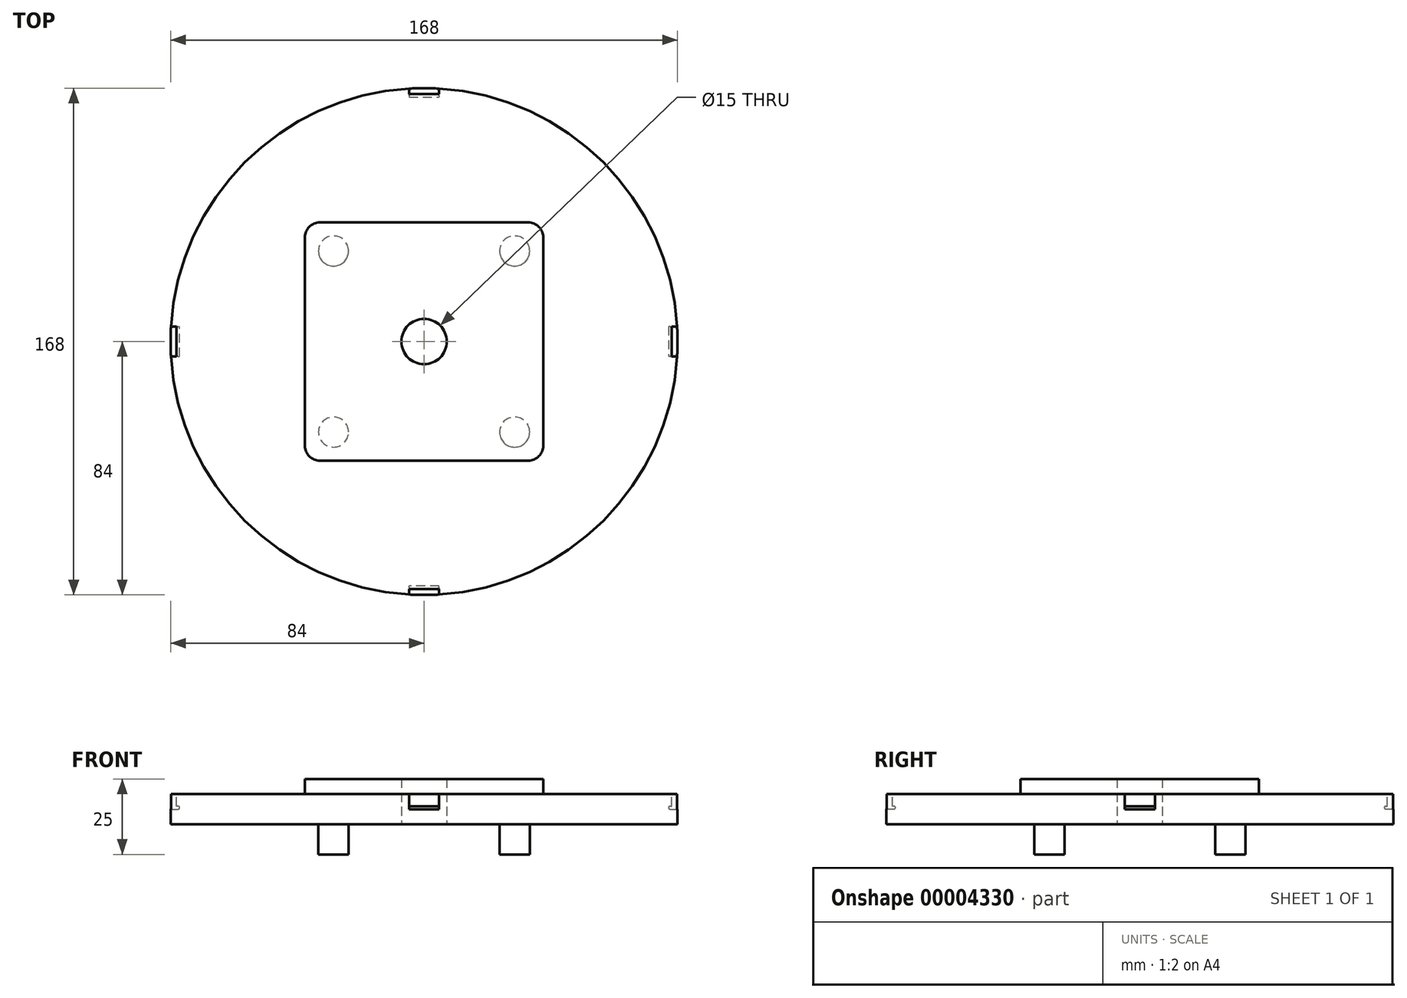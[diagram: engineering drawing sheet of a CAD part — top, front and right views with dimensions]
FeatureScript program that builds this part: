
annotation { "Feature Type Name" : "Feature", "Feature Type Description" : "" }
export const myFeature = defineFeature(function(context is Context, id is Id, definition is map)
    precondition{}
    {
        {
            var Q0;
            Q0=qCreatedBy(makeId("Top.planeOp"),FACE);
            var sketch = newSketch(context, id + "F0", { "sketchPlane" : qUnion([Q0])});
            skCircle(sketch, "E0", {"center": v(0, 0) * mm, "radius": 90 * mm});
            skSolve(sketch);
        }
        {
            var Q0;
            Q0=makeQuery(id+"F0.imprint","IMPRINT",FACE,{"disambiguationData":[TD([[makeQuery(id+"F0.imprint","IMPRINT",EDGE,{"derivedFrom":sQuery(id+"F0.wireOp",EDGE,"E0")}),1.0]])]});
            extrude(context, id + "F1", {"entities" : qUnion([Q0]), "depth" : 10 * mm});
        }
        {
            var Q0;
            Q0=makeQuery(id+"F1.opExtrude","CAP_FACE",FACE,{"disambiguationData":[OSD([sQuery(id+"F0.wireOp",EDGE,"E0")])],"isStart":false});
            var sketch = newSketch(context, id + "F2", { "sketchPlane" : qUnion([Q0])});
            skCircle(sketch, "E1.0", {"center": v(0, 0) * mm, "radius": 80 * mm});
            skLineSegment(sketch, "E2", {"start": v(0, 0) * mm, "end": v(-40, 0) * mm});
            skLineSegment(sketch, "E3", {"start": v(0, 0) * mm, "end": v(40, 0) * mm});
            skLineSegment(sketch, "E4", {"start": v(0, 0) * mm, "end": v(0, 40) * mm});
            skLineSegment(sketch, "E5", {"start": v(0, 0) * mm, "end": v(0, -40) * mm});
            skLineSegment(sketch, "E6", {"start": v(-40, -35) * mm, "end": v(-40, 35) * mm});
            skPoint(sketch, "E7.visualSharp", {"position": v(-40, 40) * mm});
            skLineSegment(sketch, "E8", {"start": v(40, 35) * mm, "end": v(40, -35) * mm});
            skPoint(sketch, "E9.visualSharp", {"position": v(40, 40) * mm});
            skPoint(sketch, "E10.visualSharp", {"position": v(40, -40) * mm});
            skPoint(sketch, "E11.visualSharp", {"position": v(-40, -40) * mm});
            skPoint(sketch, "E12.visualSharp", {"position": v(-40, -35) * mm});
            skPoint(sketch, "E13.visualSharp", {"position": v(40, -35) * mm});
            skPoint(sketch, "E14.visualSharp", {"position": v(40, 35) * mm});
            skPoint(sketch, "E15.visualSharp", {"position": v(-40, 35) * mm});
            skLineSegment(sketch, "E16.0", {"start": v(0, 40) * mm, "end": v(-35, 40) * mm});
            skLineSegment(sketch, "E17.0", {"start": v(0, 40) * mm, "end": v(35, 40) * mm});
            skLineSegment(sketch, "E18.0", {"start": v(0, -40) * mm, "end": v(35, -40) * mm});
            skLineSegment(sketch, "E19.0", {"start": v(0, -40) * mm, "end": v(-35, -40) * mm});
            skArc(sketch, "E20.filletArc", {"start": v(-40, -35) * mm, "mid": v(-38.54, -38.54) * mm, "end": v(-35, -40) * mm});
            skArc(sketch, "E21.filletArc", {"start": v(35, -40) * mm, "mid": v(38.54, -38.54) * mm, "end": v(40, -35) * mm});
            skArc(sketch, "E22.filletArc", {"start": v(40, 35) * mm, "mid": v(38.54, 38.54) * mm, "end": v(35, 40) * mm});
            skArc(sketch, "E23.filletArc", {"start": v(-35, 40) * mm, "mid": v(-38.54, 38.54) * mm, "end": v(-40, 35) * mm});
            skLineSegment(sketch, "E24.0", {"start": v(-39.5, -34.5) * mm, "end": v(-39.5, 34.5) * mm});
            skLineSegment(sketch, "E24.1", {"start": v(0, -39.5) * mm, "end": v(-34.5, -39.5) * mm});
            skLineSegment(sketch, "E24.2", {"start": v(0, -39.5) * mm, "end": v(34.5, -39.5) * mm});
            skLineSegment(sketch, "E24.3", {"start": v(39.5, 34.5) * mm, "end": v(39.5, -34.5) * mm});
            skLineSegment(sketch, "E24.4", {"start": v(0, 39.5) * mm, "end": v(34.5, 39.5) * mm});
            skLineSegment(sketch, "E24.5", {"start": v(0, 39.5) * mm, "end": v(-34.5, 39.5) * mm});
            skPoint(sketch, "E25.visualSharp", {"position": v(-39.5, 39.5) * mm});
            skArc(sketch, "E25.filletArc", {"start": v(-34.5, 39.5) * mm, "mid": v(-38.04, 38.04) * mm, "end": v(-39.5, 34.5) * mm});
            skPoint(sketch, "E26.visualSharp", {"position": v(-39.5, -39.5) * mm});
            skArc(sketch, "E26.filletArc", {"start": v(-39.5, -34.5) * mm, "mid": v(-38.04, -38.04) * mm, "end": v(-34.5, -39.5) * mm});
            skPoint(sketch, "E27.visualSharp", {"position": v(39.5, -39.5) * mm});
            skArc(sketch, "E27.filletArc", {"start": v(34.5, -39.5) * mm, "mid": v(38.04, -38.04) * mm, "end": v(39.5, -34.5) * mm});
            skPoint(sketch, "E28.visualSharp", {"position": v(39.5, 39.5) * mm});
            skArc(sketch, "E28.filletArc", {"start": v(39.5, 34.5) * mm, "mid": v(38.04, 38.04) * mm, "end": v(34.5, 39.5) * mm});
            skSolve(sketch);
        }
        {
            var Q0;
            Q0=makeQuery(id+"F1.opExtrude","CAP_FACE",FACE,{"disambiguationData":[OSD([sQuery(id+"F0.wireOp",EDGE,"E0")])],"isStart":true});
            var sketch = newSketch(context, id + "F3", { "sketchPlane" : qUnion([Q0])});
            skCircle(sketch, "E29.0", {"center": v(0, 0) * mm, "radius": 84 * mm});
            skSolve(sketch);
        }
        {
            var Q0;
            Q0=makeQuery(id+"F3.imprint","IMPRINT",FACE,{"disambiguationData":[TD([[makeQuery(id+"F3.imprint","IMPRINT",EDGE,{"derivedFrom":sQuery(id+"F3.wireOp",EDGE,"E29.0")}),-1.0]])]});
            extrude(context, id + "F4", {"entities" : qUnion([Q0]), "operationType" : NewBodyOperationType.REMOVE, "oppositeDirection" : true, "depth" : 25 * mm});
        }
        {
            var Q0;
            Q0=makeQuery(id+"F1.opExtrude","CAP_FACE",FACE,{"disambiguationData":[OSD([sQuery(id+"F0.wireOp",EDGE,"E0")])],"isStart":false});
            var sketch = newSketch(context, id + "F5", { "sketchPlane" : qUnion([Q0])});
            skLineSegment(sketch, "E30.0", {"start": v(5, 82) * mm, "end": v(-5, 82) * mm});
            skLineSegment(sketch, "E31.0", {"start": v(5, 84) * mm, "end": v(-5, 84) * mm});
            skLineSegment(sketch, "E32", {"start": v(-5, 84) * mm, "end": v(-5, 82) * mm});
            skLineSegment(sketch, "E33", {"start": v(5, 84) * mm, "end": v(5, 82) * mm});
            skLineSegment(sketch, "E34.0", {"start": v(-84, 5) * mm, "end": v(-84, -5) * mm});
            skLineSegment(sketch, "E35.0", {"start": v(-82, 5) * mm, "end": v(-82, -5) * mm});
            skLineSegment(sketch, "E36", {"start": v(-84, -5) * mm, "end": v(-82, -5) * mm});
            skLineSegment(sketch, "E37", {"start": v(-84, 5) * mm, "end": v(-82, 5) * mm});
            skLineSegment(sketch, "E38.0", {"start": v(5, -84) * mm, "end": v(-5, -84) * mm});
            skLineSegment(sketch, "E39.0", {"start": v(5, -82) * mm, "end": v(-5, -82) * mm});
            skLineSegment(sketch, "E40", {"start": v(-5, -82) * mm, "end": v(-5, -84) * mm});
            skLineSegment(sketch, "E41", {"start": v(5, -82) * mm, "end": v(5, -84) * mm});
            skLineSegment(sketch, "E42.0", {"start": v(84, 5) * mm, "end": v(84, -5) * mm});
            skLineSegment(sketch, "E43.0", {"start": v(82, 5) * mm, "end": v(82, -5) * mm});
            skLineSegment(sketch, "E44", {"start": v(82, -5) * mm, "end": v(84, -5) * mm});
            skLineSegment(sketch, "E45", {"start": v(82, 5) * mm, "end": v(84, 5) * mm});
            skSolve(sketch);
        }
        {
            var Q0;
            {var subQ2=sQuery(id+"F2.wireOp",EDGE,"E2");Q0=makeQuery(id+"F2.imprint","IMPRINT",FACE,{"disambiguationData":[TD([[makeQuery(id+"F2.imprint","IMPRINT",EDGE,{"derivedFrom":subQ2}),-1.0]])]});}
            var Q1;
            {var subQ2=sQuery(id+"F2.wireOp",EDGE,"E3");Q1=makeQuery(id+"F2.imprint","IMPRINT",FACE,{"disambiguationData":[TD([[makeQuery(id+"F2.imprint","IMPRINT",EDGE,{"derivedFrom":subQ2}),1.0]])]});}
            var Q2;
            {var subQ2=sQuery(id+"F2.wireOp",EDGE,"E3");Q2=makeQuery(id+"F2.imprint","IMPRINT",FACE,{"disambiguationData":[TD([[makeQuery(id+"F2.imprint","IMPRINT",EDGE,{"derivedFrom":subQ2}),-1.0]])]});}
            var Q3;
            {var subQ2=sQuery(id+"F2.wireOp",EDGE,"E2");Q3=makeQuery(id+"F2.imprint","IMPRINT",FACE,{"disambiguationData":[TD([[makeQuery(id+"F2.imprint","IMPRINT",EDGE,{"derivedFrom":subQ2}),1.0]])]});}
            extrude(context, id + "F6", {"entities" : qUnion([Q0, Q1, Q2, Q3]), "operationType" : NewBodyOperationType.ADD, "depth" : 5 * mm});
        }
        {
            var Q0;
            Q0=makeQuery(id+"F1.opExtrude","CAP_FACE",FACE,{"disambiguationData":[OSD([sQuery(id+"F0.wireOp",EDGE,"E0")])],"isStart":true});
            var sketch = newSketch(context, id + "F7", { "sketchPlane" : qUnion([Q0])});
            skLineSegment(sketch, "E46", {"start": v(0, 0) * mm, "end": v(0, 30) * mm});
            skLineSegment(sketch, "E47", {"start": v(0, 0) * mm, "end": v(0, -30) * mm});
            skLineSegment(sketch, "E48", {"start": v(0, 0) * mm, "end": v(-30, 0) * mm});
            skLineSegment(sketch, "E49", {"start": v(0, 0) * mm, "end": v(30, 0) * mm});
            skLineSegment(sketch, "E50.0", {"start": v(30, 0) * mm, "end": v(30, 30) * mm});
            skLineSegment(sketch, "E51.0", {"start": v(-30, 0) * mm, "end": v(-30, 30) * mm});
            skLineSegment(sketch, "E52.0", {"start": v(0, 30) * mm, "end": v(-30, 30) * mm});
            skLineSegment(sketch, "E53.0", {"start": v(0, 30) * mm, "end": v(30, 30) * mm});
            skLineSegment(sketch, "E54.0", {"start": v(-30, 0) * mm, "end": v(-30, -30) * mm});
            skLineSegment(sketch, "E55.0", {"start": v(30, 0) * mm, "end": v(30, -30) * mm});
            skLineSegment(sketch, "E56.0", {"start": v(0, -30) * mm, "end": v(-30, -30) * mm});
            skLineSegment(sketch, "E57.0", {"start": v(0, -30) * mm, "end": v(30, -30) * mm});
            skCircle(sketch, "E58", {"center": v(-30, 30) * mm, "radius": 5 * mm});
            skCircle(sketch, "E59", {"center": v(30, 30) * mm, "radius": 5 * mm});
            skCircle(sketch, "E60", {"center": v(-30, -30) * mm, "radius": 5 * mm});
            skCircle(sketch, "E61", {"center": v(30, -30) * mm, "radius": 5 * mm});
            skSolve(sketch);
        }
        {
            var Q0;
            {var subQ1=sQuery(id+"F7.wireOp",EDGE,"E52.0");var subQ3=sQuery(id+"F7.wireOp",EDGE,"E51.0");var subQ5=makeQuery(id+"F7.imprint","INTERSECT",VERTEX,{"derivedFrom":[subQ3,subQ1]});Q0=makeQuery(id+"F7.imprint","IMPRINT",FACE,{"disambiguationData":[TD([[makeQuery(id+"F7.imprint","IMPRINT",EDGE,{"disambiguationData":[TD([[subQ5,1.0]])],"derivedFrom":subQ3}),1.0]])]});}
            var Q1;
            {var subQ1=sQuery(id+"F7.wireOp",EDGE,"E52.0");var subQ3=sQuery(id+"F7.wireOp",EDGE,"E51.0");var subQ5=makeQuery(id+"F7.imprint","INTERSECT",VERTEX,{"derivedFrom":[subQ3,subQ1]});Q1=makeQuery(id+"F7.imprint","IMPRINT",FACE,{"disambiguationData":[TD([[makeQuery(id+"F7.imprint","IMPRINT",EDGE,{"disambiguationData":[TD([[subQ5,1.0]])],"derivedFrom":subQ3}),-1.0]])]});}
            var Q2;
            {var subQ1=sQuery(id+"F7.wireOp",EDGE,"E53.0");var subQ3=sQuery(id+"F7.wireOp",EDGE,"E50.0");var subQ5=makeQuery(id+"F7.imprint","INTERSECT",VERTEX,{"derivedFrom":[subQ3,subQ1]});Q2=makeQuery(id+"F7.imprint","IMPRINT",FACE,{"disambiguationData":[TD([[makeQuery(id+"F7.imprint","IMPRINT",EDGE,{"disambiguationData":[TD([[subQ5,1.0]])],"derivedFrom":subQ3}),-1.0]])]});}
            var Q3;
            {var subQ1=sQuery(id+"F7.wireOp",EDGE,"E53.0");var subQ3=sQuery(id+"F7.wireOp",EDGE,"E50.0");var subQ5=makeQuery(id+"F7.imprint","INTERSECT",VERTEX,{"derivedFrom":[subQ3,subQ1]});Q3=makeQuery(id+"F7.imprint","IMPRINT",FACE,{"disambiguationData":[TD([[makeQuery(id+"F7.imprint","IMPRINT",EDGE,{"disambiguationData":[TD([[subQ5,1.0]])],"derivedFrom":subQ3}),1.0]])]});}
            var Q4;
            {var subQ1=sQuery(id+"F7.wireOp",EDGE,"E56.0");var subQ3=sQuery(id+"F7.wireOp",EDGE,"E54.0");var subQ5=makeQuery(id+"F7.imprint","INTERSECT",VERTEX,{"derivedFrom":[subQ3,subQ1]});Q4=makeQuery(id+"F7.imprint","IMPRINT",FACE,{"disambiguationData":[TD([[makeQuery(id+"F7.imprint","IMPRINT",EDGE,{"disambiguationData":[TD([[subQ5,1.0]])],"derivedFrom":subQ3}),-1.0]])]});}
            var Q5;
            {var subQ1=sQuery(id+"F7.wireOp",EDGE,"E56.0");var subQ3=sQuery(id+"F7.wireOp",EDGE,"E54.0");var subQ5=makeQuery(id+"F7.imprint","INTERSECT",VERTEX,{"derivedFrom":[subQ3,subQ1]});Q5=makeQuery(id+"F7.imprint","IMPRINT",FACE,{"disambiguationData":[TD([[makeQuery(id+"F7.imprint","IMPRINT",EDGE,{"disambiguationData":[TD([[subQ5,1.0]])],"derivedFrom":subQ3}),1.0]])]});}
            var Q6;
            {var subQ1=sQuery(id+"F7.wireOp",EDGE,"E57.0");var subQ3=sQuery(id+"F7.wireOp",EDGE,"E55.0");var subQ5=makeQuery(id+"F7.imprint","INTERSECT",VERTEX,{"derivedFrom":[subQ3,subQ1]});Q6=makeQuery(id+"F7.imprint","IMPRINT",FACE,{"disambiguationData":[TD([[makeQuery(id+"F7.imprint","IMPRINT",EDGE,{"disambiguationData":[TD([[subQ5,1.0]])],"derivedFrom":subQ3}),-1.0]])]});}
            var Q7;
            {var subQ1=sQuery(id+"F7.wireOp",EDGE,"E57.0");var subQ3=sQuery(id+"F7.wireOp",EDGE,"E55.0");var subQ5=makeQuery(id+"F7.imprint","INTERSECT",VERTEX,{"derivedFrom":[subQ3,subQ1]});Q7=makeQuery(id+"F7.imprint","IMPRINT",FACE,{"disambiguationData":[TD([[makeQuery(id+"F7.imprint","IMPRINT",EDGE,{"disambiguationData":[TD([[subQ5,1.0]])],"derivedFrom":subQ3}),1.0]])]});}
            extrude(context, id + "F8", {"entities" : qUnion([Q0, Q1, Q2, Q3, Q4, Q5, Q6, Q7]), "operationType" : NewBodyOperationType.ADD, "depth" : 10 * mm});
        }
        {
            var Q0;
            {var subQ6=sQuery(id+"F5.wireOp",EDGE,"E35.0");Q0=makeQuery(id+"F5.imprint","IMPRINT",FACE,{"disambiguationData":[TD([[makeQuery(id+"F5.imprint","IMPRINT",EDGE,{"derivedFrom":subQ6}),-1.0]])]});}
            var Q1;
            {var subQ6=sQuery(id+"F5.wireOp",EDGE,"E39.0");Q1=makeQuery(id+"F5.imprint","IMPRINT",FACE,{"disambiguationData":[TD([[makeQuery(id+"F5.imprint","IMPRINT",EDGE,{"derivedFrom":subQ6}),1.0]])]});}
            var Q2;
            {var subQ6=sQuery(id+"F5.wireOp",EDGE,"E43.0");Q2=makeQuery(id+"F5.imprint","IMPRINT",FACE,{"disambiguationData":[TD([[makeQuery(id+"F5.imprint","IMPRINT",EDGE,{"derivedFrom":subQ6}),1.0]])]});}
            var Q3;
            {var subQ6=sQuery(id+"F5.wireOp",EDGE,"E30.0");Q3=makeQuery(id+"F5.imprint","IMPRINT",FACE,{"disambiguationData":[TD([[makeQuery(id+"F5.imprint","IMPRINT",EDGE,{"derivedFrom":subQ6}),-1.0]])]});}
            extrude(context, id + "F9", {"entities" : qUnion([Q0, Q1, Q2, Q3]), "operationType" : NewBodyOperationType.REMOVE, "oppositeDirection" : true, "depth" : 5 * mm});
        }
        {
            var Q0;
            Q0=makeQuery(id+"F9.boolean.opBoolean","COPY",FACE,{"derivedFrom":makeQuery(id+"F9.opExtrude","SWEPT_FACE",FACE,{"disambiguationData":[OSD([sQuery(id+"F5.wireOp",EDGE,"E30.0")])]})});
            var sketch = newSketch(context, id + "F10", { "sketchPlane" : qUnion([Q0])});
            skLineSegment(sketch, "E62.0", {"start": v(-5, 6) * mm, "end": v(5, 6) * mm});
            skSolve(sketch);
        }
        {
            var Q0;
            Q0=makeQuery(id+"F9.boolean.opBoolean","COPY",FACE,{"derivedFrom":makeQuery(id+"F9.opExtrude","SWEPT_FACE",FACE,{"disambiguationData":[OSD([sQuery(id+"F5.wireOp",EDGE,"E35.0")])]})});
            var sketch = newSketch(context, id + "F11", { "sketchPlane" : qUnion([Q0])});
            skLineSegment(sketch, "E63.0", {"start": v(-5, 6) * mm, "end": v(5, 6) * mm});
            skSolve(sketch);
        }
        {
            var Q0;
            Q0=makeQuery(id+"F9.boolean.opBoolean","COPY",FACE,{"derivedFrom":makeQuery(id+"F9.opExtrude","SWEPT_FACE",FACE,{"disambiguationData":[OSD([sQuery(id+"F5.wireOp",EDGE,"E39.0")])]})});
            var sketch = newSketch(context, id + "F12", { "sketchPlane" : qUnion([Q0])});
            skLineSegment(sketch, "E64.0", {"start": v(5, 6) * mm, "end": v(-5, 6) * mm});
            skSolve(sketch);
        }
        {
            var Q0;
            Q0=makeQuery(id+"F9.boolean.opBoolean","COPY",FACE,{"derivedFrom":makeQuery(id+"F9.opExtrude","SWEPT_FACE",FACE,{"disambiguationData":[OSD([sQuery(id+"F5.wireOp",EDGE,"E43.0")])]})});
            var sketch = newSketch(context, id + "F13", { "sketchPlane" : qUnion([Q0])});
            skLineSegment(sketch, "E65.0", {"start": v(5, 6) * mm, "end": v(-5, 6) * mm});
            skSolve(sketch);
        }
        {
            var Q0;
            {var subQ2=sQuery(id+"F10.wireOp",EDGE,"E62.0");Q0=makeQuery(id+"F10.imprint","IMPRINT",FACE,{"disambiguationData":[TD([[makeQuery(id+"F10.imprint","IMPRINT",EDGE,{"derivedFrom":subQ2}),-1.0]])]});}
            extrude(context, id + "F14", {"entities" : qUnion([Q0]), "operationType" : NewBodyOperationType.REMOVE, "oppositeDirection" : true, "depth" : 1 * mm});
        }
        {
            var Q0;
            {var subQ2=sQuery(id+"F11.wireOp",EDGE,"E63.0");Q0=makeQuery(id+"F11.imprint","IMPRINT",FACE,{"disambiguationData":[TD([[makeQuery(id+"F11.imprint","IMPRINT",EDGE,{"derivedFrom":subQ2}),-1.0]])]});}
            extrude(context, id + "F15", {"entities" : qUnion([Q0]), "operationType" : NewBodyOperationType.REMOVE, "oppositeDirection" : true, "depth" : 1 * mm});
        }
        {
            var Q0;
            {var subQ2=sQuery(id+"F12.wireOp",EDGE,"E64.0");Q0=makeQuery(id+"F12.imprint","IMPRINT",FACE,{"disambiguationData":[TD([[makeQuery(id+"F12.imprint","IMPRINT",EDGE,{"derivedFrom":subQ2}),1.0]])]});}
            extrude(context, id + "F16", {"entities" : qUnion([Q0]), "operationType" : NewBodyOperationType.REMOVE, "oppositeDirection" : true, "depth" : 1 * mm});
        }
        {
            var Q0;
            {var subQ2=sQuery(id+"F13.wireOp",EDGE,"E65.0");Q0=makeQuery(id+"F13.imprint","IMPRINT",FACE,{"disambiguationData":[TD([[makeQuery(id+"F13.imprint","IMPRINT",EDGE,{"derivedFrom":subQ2}),1.0]])]});}
            extrude(context, id + "F17", {"entities" : qUnion([Q0]), "operationType" : NewBodyOperationType.REMOVE, "oppositeDirection" : true, "depth" : 1 * mm});
        }
        {
            var Q0;
            Q0=makeQuery(id+"F14.boolean.opBoolean","COPY",EDGE,{"derivedFrom":makeQuery(id+"F14.opExtrude","CAP_EDGE",EDGE,{"disambiguationData":[OSD([sQuery(id+"F5.wireOp",EDGE,"E30.0")])],"isStart":false})});
            var Q1;
            Q1=makeQuery(id+"F14.boolean.opBoolean","COPY",EDGE,{"derivedFrom":makeQuery(id+"F14.opExtrude","CAP_EDGE",EDGE,{"disambiguationData":[OSD([sQuery(id+"F10.wireOp",EDGE,"E62.0")])],"isStart":false})});
            fillet(context, id + "F18", {"entities" : qUnion([Q0, Q1]), "radius" : 0.5 * mm, "tangentPropagation" : true, "allowEdgeOverflow" : false});
        }
        {
            var Q0;
            Q0=makeQuery(id+"F15.boolean.opBoolean","COPY",EDGE,{"derivedFrom":makeQuery(id+"F15.opExtrude","CAP_EDGE",EDGE,{"disambiguationData":[OSD([sQuery(id+"F5.wireOp",EDGE,"E35.0")])],"isStart":false})});
            var Q1;
            Q1=makeQuery(id+"F15.boolean.opBoolean","COPY",EDGE,{"derivedFrom":makeQuery(id+"F15.opExtrude","CAP_EDGE",EDGE,{"disambiguationData":[OSD([sQuery(id+"F11.wireOp",EDGE,"E63.0")])],"isStart":false})});
            fillet(context, id + "F19", {"entities" : qUnion([Q0, Q1]), "radius" : 0.5 * mm, "tangentPropagation" : true, "allowEdgeOverflow" : false});
        }
        {
            var Q0;
            Q0=makeQuery(id+"F16.boolean.opBoolean","COPY",EDGE,{"derivedFrom":makeQuery(id+"F16.opExtrude","CAP_EDGE",EDGE,{"disambiguationData":[OSD([sQuery(id+"F12.wireOp",EDGE,"E64.0")])],"isStart":false})});
            var Q1;
            Q1=makeQuery(id+"F16.boolean.opBoolean","COPY",EDGE,{"derivedFrom":makeQuery(id+"F16.opExtrude","CAP_EDGE",EDGE,{"disambiguationData":[OSD([sQuery(id+"F5.wireOp",EDGE,"E39.0")])],"isStart":false})});
            fillet(context, id + "F20", {"entities" : qUnion([Q0, Q1]), "radius" : 0.5 * mm, "tangentPropagation" : true, "allowEdgeOverflow" : false});
        }
        {
            var Q0;
            Q0=makeQuery(id+"F17.boolean.opBoolean","COPY",EDGE,{"derivedFrom":makeQuery(id+"F17.opExtrude","CAP_EDGE",EDGE,{"disambiguationData":[OSD([sQuery(id+"F13.wireOp",EDGE,"E65.0")])],"isStart":false})});
            var Q1;
            Q1=makeQuery(id+"F17.boolean.opBoolean","COPY",EDGE,{"derivedFrom":makeQuery(id+"F17.opExtrude","CAP_EDGE",EDGE,{"disambiguationData":[OSD([sQuery(id+"F5.wireOp",EDGE,"E43.0")])],"isStart":false})});
            fillet(context, id + "F21", {"entities" : qUnion([Q0, Q1]), "radius" : 0.5 * mm, "tangentPropagation" : true, "allowEdgeOverflow" : false});
        }
        {
            var Q0;
            Q0=makeQuery(id+"F1.opExtrude","CAP_FACE",FACE,{"disambiguationData":[OSD([sQuery(id+"F0.wireOp",EDGE,"E0")])],"isStart":true});
            var sketch = newSketch(context, id + "F22", { "sketchPlane" : qUnion([Q0])});
            skCircle(sketch, "E66", {"center": v(0, 0) * mm, "radius": 7.5 * mm});
            skCircle(sketch, "E67.0", {"center": v(0, 0) * mm, "radius": 82 * mm});
            skSolve(sketch);
        }
        {
            var Q0;
            Q0=makeQuery(id+"F22.imprint","IMPRINT",FACE,{"disambiguationData":[TD([[makeQuery(id+"F22.imprint","IMPRINT",EDGE,{"derivedFrom":sQuery(id+"F22.wireOp",EDGE,"E66")}),1.0]])]});
            extrude(context, id + "F23", {"entities" : qUnion([Q0]), "operationType" : NewBodyOperationType.REMOVE, "oppositeDirection" : true, "depth" : 18.82 * mm});
        }
    });
